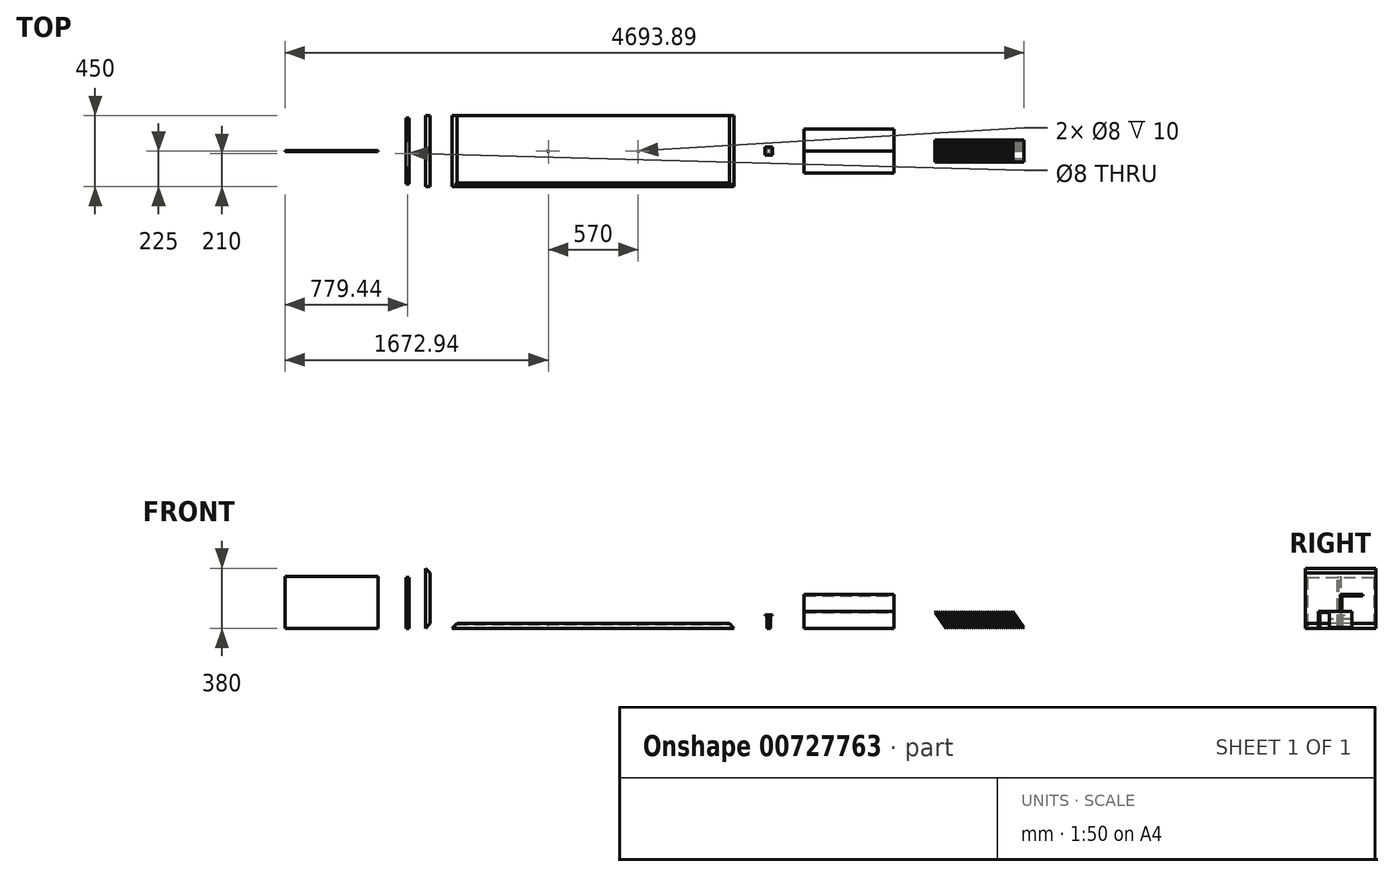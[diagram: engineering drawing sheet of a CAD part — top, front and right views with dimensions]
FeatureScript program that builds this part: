
annotation { "Feature Type Name" : "Feature", "Feature Type Description" : "" }
export const myFeature = defineFeature(function(context is Context, id is Id, definition is map)
    precondition{}
    {
        {
            var Q0;
            Q0=qCreatedBy(makeId("Top.planeOp"),FACE);
            var sketch = newSketch(context, id + "F0", { "sketchPlane" : qUnion([Q0])});
            skLineSegment(sketch, "E0.bottom", {"start": v(-895, -225) * mm, "end": v(895, -225) * mm});
            skLineSegment(sketch, "E0.top", {"start": v(-895, 225) * mm, "end": v(895, 225) * mm});
            skLineSegment(sketch, "E0.left", {"start": v(-895, -225) * mm, "end": v(-895, 225) * mm});
            skLineSegment(sketch, "E0.right", {"start": v(895, -225) * mm, "end": v(895, 225) * mm});
            skPoint(sketch, "E0.middle", {"position": v(0, 0) * mm});
            skSolve(sketch);
        }
        {
            var Q0;
            Q0 = qSketchRegion(id + "F0", true);
            extrude(context, id + "F1", {"entities" : qUnion([Q0]), "depth" : 29 * mm, "offsetDistance" : 25 * mm});
        }
        {
            var Q0;
            Q0=makeQuery(id+"F1.opExtrude","SWEPT_FACE",FACE,{"disambiguationData":[OSD([sQuery(id+"F0.wireOp",EDGE,"E0.bottom")])]});
            var sketch = newSketch(context, id + "F2", { "sketchPlane" : qUnion([Q0])});
            skLineSegment(sketch, "E1", {"start": v(-895, 0) * mm, "end": v(-895, 29) * mm});
            skLineSegment(sketch, "E2", {"start": v(-895, 29) * mm, "end": v(-866, 29) * mm});
            skLineSegment(sketch, "E3", {"start": v(-866, 29) * mm, "end": v(-895, 0) * mm});
            skLineSegment(sketch, "E4", {"start": v(895, 0) * mm, "end": v(895, 29) * mm});
            skLineSegment(sketch, "E5", {"start": v(895, 29) * mm, "end": v(866, 29) * mm});
            skLineSegment(sketch, "E6", {"start": v(866, 29) * mm, "end": v(895, 0) * mm});
            skSolve(sketch);
        }
        {
            var Q0;
            Q0 = qSketchRegion(id + "F2", true);
            extrude(context, id + "F3", {"entities" : qUnion([Q0]), "operationType" : NewBodyOperationType.REMOVE, "oppositeDirection" : true, "depth" : 450 * mm, "offsetDistance" : 25 * mm});
        }
        {
            var Q0;
            Q0=qCreatedBy(makeId("Right.planeOp"),FACE);
            var sketch = newSketch(context, id + "F4", { "sketchPlane" : qUnion([Q0])});
            skLineSegment(sketch, "E7.bottom", {"start": v(-220, 29) * mm, "end": v(-202, 29) * mm});
            skLineSegment(sketch, "E7.top", {"start": v(-220, 24) * mm, "end": v(-202, 24) * mm});
            skLineSegment(sketch, "E7.left", {"start": v(-220, 29) * mm, "end": v(-220, 24) * mm});
            skLineSegment(sketch, "E7.right", {"start": v(-202, 29) * mm, "end": v(-202, 24) * mm});
            skSolve(sketch);
        }
        {
            var Q0;
            Q0 = qSketchRegion(id + "F4", true);
            extrude(context, id + "F5", {"entities" : qUnion([Q0]), "operationType" : NewBodyOperationType.REMOVE, "oppositeDirection" : true, "depth" : 1790 * mm, "offsetDistance" : 25 * mm, "symmetric" : true});
        }
        {
            var Q0;
            {var subQ0=sQuery(id+"F0.wireOp",EDGE,"E0.top");Q0=makeQuery(id+"F5.boolean.opBoolean","SPLIT",FACE,{"disambiguationData":[TD([makeQuery(id+"F1.opExtrude","SWEPT_FACE",FACE,{"disambiguationData":[OSD([subQ0])]})])],"derivedFrom":makeQuery(id+"F1.opExtrude","CAP_FACE",FACE,{"disambiguationData":[OSD([sQuery(id+"F0.wireOp",EDGE,"E0.bottom"),subQ0,sQuery(id+"F0.wireOp",EDGE,"E0.left"),sQuery(id+"F0.wireOp",EDGE,"E0.right")])],"isStart":false})});}
            var sketch = newSketch(context, id + "F6", { "sketchPlane" : qUnion([Q0])});
            skCircle(sketch, "E8", {"center": v(-285, 0) * mm, "radius": 4 * mm});
            skCircle(sketch, "E9", {"center": v(285, 0) * mm, "radius": 4 * mm});
            skSolve(sketch);
        }
        {
            var Q0;
            Q0 = qSketchRegion(id + "F6", true);
            extrude(context, id + "F7", {"entities" : qUnion([Q0]), "operationType" : NewBodyOperationType.REMOVE, "oppositeDirection" : true, "depth" : 10 * mm, "offsetDistance" : 25 * mm});
        }
        {
            var Q0;
            Q0=qCreatedBy(makeId("Top.planeOp"),FACE);
            var sketch = newSketch(context, id + "F8", { "sketchPlane" : qUnion([Q0])});
            skLineSegment(sketch, "E10.bottom", {"start": v(-1064.12, -225) * mm, "end": v(-1035.12, -225) * mm});
            skLineSegment(sketch, "E10.top", {"start": v(-1064.12, 225) * mm, "end": v(-1035.12, 225) * mm});
            skLineSegment(sketch, "E10.left", {"start": v(-1064.12, -225) * mm, "end": v(-1064.12, 225) * mm});
            skLineSegment(sketch, "E10.right", {"start": v(-1035.12, -225) * mm, "end": v(-1035.12, 225) * mm});
            skPoint(sketch, "E10.middle", {"position": v(-1049.62, 0) * mm});
            skSolve(sketch);
        }
        {
            var Q0;
            Q0 = qSketchRegion(id + "F8", true);
            extrude(context, id + "F9", {"entities" : qUnion([Q0]), "depth" : 380 * mm, "offsetDistance" : 25 * mm});
        }
        {
            var Q0;
            Q0=makeQuery(id+"F9.opExtrude","SWEPT_FACE",FACE,{"disambiguationData":[OSD([sQuery(id+"F8.wireOp",EDGE,"E10.bottom")])]});
            var sketch = newSketch(context, id + "F10", { "sketchPlane" : qUnion([Q0])});
            skLineSegment(sketch, "E11", {"start": v(-1035.12, 380) * mm, "end": v(-1064.12, 380) * mm});
            skLineSegment(sketch, "E12", {"start": v(-1035.12, 380) * mm, "end": v(-1035.12, 351) * mm});
            skLineSegment(sketch, "E13", {"start": v(-1035.12, 351) * mm, "end": v(-1064.12, 380) * mm});
            skLineSegment(sketch, "E14", {"start": v(-1064.12, 0) * mm, "end": v(-1035.12, 0) * mm});
            skLineSegment(sketch, "E15", {"start": v(-1035.12, 0) * mm, "end": v(-1035.12, 29) * mm});
            skLineSegment(sketch, "E16", {"start": v(-1035.12, 29) * mm, "end": v(-1064.12, 0) * mm});
            skSolve(sketch);
        }
        {
            var Q0;
            Q0 = qSketchRegion(id + "F10", true);
            extrude(context, id + "F11", {"entities" : qUnion([Q0]), "operationType" : NewBodyOperationType.REMOVE, "oppositeDirection" : true, "depth" : 450 * mm, "offsetDistance" : 25 * mm});
        }
        {
            var Q0;
            Q0=qCreatedBy(makeId("Top.planeOp"),FACE);
            var sketch = newSketch(context, id + "F12", { "sketchPlane" : qUnion([Q0])});
            skLineSegment(sketch, "E17.bottom", {"start": v(-1188.5, -210) * mm, "end": v(-1168.5, -210) * mm});
            skLineSegment(sketch, "E17.top", {"start": v(-1188.5, 210) * mm, "end": v(-1168.5, 210) * mm});
            skLineSegment(sketch, "E17.left", {"start": v(-1188.5, -210) * mm, "end": v(-1188.5, 210) * mm});
            skLineSegment(sketch, "E17.right", {"start": v(-1168.5, -210) * mm, "end": v(-1168.5, 210) * mm});
            skPoint(sketch, "E17.middle", {"position": v(-1178.5, 0) * mm});
            skSolve(sketch);
        }
        {
            var Q0;
            Q0 = qSketchRegion(id + "F12", true);
            extrude(context, id + "F13", {"entities" : qUnion([Q0]), "depth" : 322 * mm, "offsetDistance" : 25 * mm});
        }
        {
            var Q0;
            Q0=makeQuery(id+"F13.opExtrude","CAP_FACE",FACE,{"disambiguationData":[OSD([sQuery(id+"F12.wireOp",EDGE,"E17.bottom"),sQuery(id+"F12.wireOp",EDGE,"E17.top"),sQuery(id+"F12.wireOp",EDGE,"E17.left"),sQuery(id+"F12.wireOp",EDGE,"E17.right")])],"isStart":false});
            var sketch = newSketch(context, id + "F14", { "sketchPlane" : qUnion([Q0])});
            skCircle(sketch, "E18", {"center": v(-1178.5, -15) * mm, "radius": 4 * mm});
            skPoint(sketch, "E18.centerSnap0", {"position": v(-1178.5, 210) * mm});
            skSolve(sketch);
        }
        {
            var Q0;
            Q0 = qSketchRegion(id + "F14", true);
            extrude(context, id + "F15", {"entities" : qUnion([Q0]), "operationType" : NewBodyOperationType.REMOVE, "oppositeDirection" : true, "depth" : 322 * mm, "offsetDistance" : 25 * mm});
        }
        {
            var Q0;
            Q0=qCreatedBy(makeId("Top.planeOp"),FACE);
            var sketch = newSketch(context, id + "F16", { "sketchPlane" : qUnion([Q0])});
            skLineSegment(sketch, "E19.bottom", {"start": v(1339.88, -140) * mm, "end": v(1910.88, -140) * mm});
            skLineSegment(sketch, "E19.top", {"start": v(1339.88, 140) * mm, "end": v(1910.88, 140) * mm});
            skLineSegment(sketch, "E19.left", {"start": v(1339.88, -140) * mm, "end": v(1339.88, 140) * mm});
            skLineSegment(sketch, "E19.right", {"start": v(1910.88, -140) * mm, "end": v(1910.88, 140) * mm});
            skPoint(sketch, "E19.middle", {"position": v(1625.38, 0) * mm});
            skSolve(sketch);
        }
        {
            var Q0;
            Q0 = qSketchRegion(id + "F16", true);
            extrude(context, id + "F17", {"entities" : qUnion([Q0]), "depth" : 322 * mm, "offsetDistance" : 25 * mm});
        }
        {
            var Q0;
            Q0=makeQuery(id+"F17.opExtrude","SWEPT_FACE",FACE,{"disambiguationData":[OSD([sQuery(id+"F16.wireOp",EDGE,"E19.right")])]});
            var sketch = newSketch(context, id + "F18", { "sketchPlane" : qUnion([Q0])});
            skLineSegment(sketch, "E20", {"start": v(-140, 107) * mm, "end": v(0, 107) * mm});
            skLineSegment(sketch, "E21", {"start": v(0, 107) * mm, "end": v(0, 214) * mm});
            skLineSegment(sketch, "E22", {"start": v(0, 214) * mm, "end": v(140, 214) * mm});
            skLineSegment(sketch, "E23", {"start": v(140, 206) * mm, "end": v(8, 206) * mm});
            skLineSegment(sketch, "E24", {"start": v(8, 206) * mm, "end": v(8, 99) * mm});
            skLineSegment(sketch, "E25", {"start": v(8, 99) * mm, "end": v(-132, 99) * mm});
            skLineSegment(sketch, "E26", {"start": v(-132, 99) * mm, "end": v(-132, 0) * mm});
            skLineSegment(sketch, "E27", {"start": v(-132, 0) * mm, "end": v(140, 0) * mm});
            skLineSegment(sketch, "E28", {"start": v(140, 0) * mm, "end": v(140, 206) * mm});
            skLineSegment(sketch, "E29", {"start": v(140, 214) * mm, "end": v(140, 322) * mm});
            skLineSegment(sketch, "E30", {"start": v(140, 322) * mm, "end": v(-140, 322) * mm});
            skLineSegment(sketch, "E31", {"start": v(-140, 322) * mm, "end": v(-140, 107) * mm});
            skSolve(sketch);
        }
        {
            var Q0;
            Q0 = qSketchRegion(id + "F18", true);
            extrude(context, id + "F19", {"entities" : qUnion([Q0]), "operationType" : NewBodyOperationType.REMOVE, "oppositeDirection" : true, "depth" : 571 * mm, "offsetDistance" : 25 * mm});
        }
        {
            var Q0;
            Q0=qCreatedBy(makeId("Top.planeOp"),FACE);
            var sketch = newSketch(context, id + "F20", { "sketchPlane" : qUnion([Q0])});
            skLineSegment(sketch, "E32.bottom", {"start": v(2170.09, -70) * mm, "end": v(2741.09, -70) * mm});
            skLineSegment(sketch, "E32.top", {"start": v(2170.09, 70) * mm, "end": v(2741.09, 70) * mm});
            skLineSegment(sketch, "E32.left", {"start": v(2170.09, -70) * mm, "end": v(2170.09, 70) * mm});
            skLineSegment(sketch, "E32.right", {"start": v(2741.09, -70) * mm, "end": v(2741.09, 70) * mm});
            skPoint(sketch, "E32.middle", {"position": v(2455.59, 0) * mm});
            skSolve(sketch);
        }
        {
            var Q0;
            Q0 = qSketchRegion(id + "F20", true);
            extrude(context, id + "F21", {"entities" : qUnion([Q0]), "depth" : 107 * mm, "offsetDistance" : 25 * mm});
        }
        {
            var Q0;
            Q0=makeQuery(id+"F21.opExtrude","SWEPT_FACE",FACE,{"disambiguationData":[OSD([sQuery(id+"F20.wireOp",EDGE,"E32.bottom")])]});
            var sketch = newSketch(context, id + "F22", { "sketchPlane" : qUnion([Q0])});
            skLineSegment(sketch, "E33", {"start": v(2170.09, 101.15) * mm, "end": v(2241.81, 0) * mm});
            skLineSegment(sketch, "E34", {"start": v(2170.09, 101.15) * mm, "end": v(2178.25, 106.94) * mm});
            skLineSegment(sketch, "E35", {"start": v(2249.97, 5.78) * mm, "end": v(2241.81, 0) * mm});
            skLineSegment(sketch, "E36", {"start": v(2178.25, 106.94) * mm, "end": v(2213.53, 57.18) * mm});
            skLineSegment(sketch, "E37", {"start": v(2249.97, 5.78) * mm, "end": v(2214.69, 55.54) * mm});
            skLineSegment(sketch, "E38", {"start": v(2214.69, 55.54) * mm, "end": v(2215.5, 56.12) * mm});
            skLineSegment(sketch, "E39", {"start": v(2213.53, 57.18) * mm, "end": v(2214.35, 57.75) * mm});
            skLineSegment(sketch, "E40", {"start": v(2214.35, 57.75) * mm, "end": v(2183.57, 101.15) * mm});
            skLineSegment(sketch, "E41", {"start": v(2183.57, 101.15) * mm, "end": v(2191.73, 106.94) * mm});
            skLineSegment(sketch, "E42", {"start": v(2191.73, 106.94) * mm, "end": v(2227.01, 57.18) * mm});
            skLineSegment(sketch, "E43", {"start": v(2215.5, 56.12) * mm, "end": v(2255.3, 0) * mm});
            skLineSegment(sketch, "E44", {"start": v(2255.3, 0) * mm, "end": v(2263.45, 5.78) * mm});
            skLineSegment(sketch, "E45", {"start": v(2263.45, 5.78) * mm, "end": v(2228.17, 55.54) * mm});
            skLineSegment(sketch, "E46.1.0.0", {"start": v(2227.85, 57.75) * mm, "end": v(2197.07, 101.15) * mm});
            skLineSegment(sketch, "E46.1.0.1", {"start": v(2205.23, 106.94) * mm, "end": v(2240.51, 57.18) * mm});
            skLineSegment(sketch, "E46.1.0.2", {"start": v(2229, 56.12) * mm, "end": v(2268.8, 0) * mm});
            skLineSegment(sketch, "E46.1.0.3", {"start": v(2276.95, 5.78) * mm, "end": v(2241.67, 55.54) * mm});
            skLineSegment(sketch, "E46.1.0.4", {"start": v(2268.8, 0) * mm, "end": v(2276.95, 5.78) * mm});
            skLineSegment(sketch, "E46.1.0.5", {"start": v(2197.07, 101.15) * mm, "end": v(2205.23, 106.94) * mm});
            skLineSegment(sketch, "E46.2.0.0", {"start": v(2241.35, 57.75) * mm, "end": v(2210.57, 101.15) * mm});
            skLineSegment(sketch, "E46.2.0.1", {"start": v(2218.73, 106.94) * mm, "end": v(2254.01, 57.18) * mm});
            skLineSegment(sketch, "E46.2.0.2", {"start": v(2242.5, 56.12) * mm, "end": v(2282.3, 0) * mm});
            skLineSegment(sketch, "E46.2.0.3", {"start": v(2290.45, 5.78) * mm, "end": v(2255.17, 55.54) * mm});
            skLineSegment(sketch, "E46.2.0.4", {"start": v(2282.3, 0) * mm, "end": v(2290.45, 5.78) * mm});
            skLineSegment(sketch, "E46.2.0.5", {"start": v(2210.57, 101.15) * mm, "end": v(2218.73, 106.94) * mm});
            skLineSegment(sketch, "E46.3.0.0", {"start": v(2254.85, 57.75) * mm, "end": v(2224.07, 101.15) * mm});
            skLineSegment(sketch, "E46.3.0.1", {"start": v(2232.23, 106.94) * mm, "end": v(2267.51, 57.18) * mm});
            skLineSegment(sketch, "E46.3.0.2", {"start": v(2256, 56.12) * mm, "end": v(2295.8, 0) * mm});
            skLineSegment(sketch, "E46.3.0.3", {"start": v(2303.95, 5.78) * mm, "end": v(2268.67, 55.54) * mm});
            skLineSegment(sketch, "E46.3.0.4", {"start": v(2295.8, 0) * mm, "end": v(2303.95, 5.78) * mm});
            skLineSegment(sketch, "E46.3.0.5", {"start": v(2224.07, 101.15) * mm, "end": v(2232.23, 106.94) * mm});
            skLineSegment(sketch, "E46.4.0.0", {"start": v(2268.35, 57.75) * mm, "end": v(2237.57, 101.15) * mm});
            skLineSegment(sketch, "E46.4.0.1", {"start": v(2245.73, 106.94) * mm, "end": v(2281.01, 57.18) * mm});
            skLineSegment(sketch, "E46.4.0.2", {"start": v(2269.5, 56.12) * mm, "end": v(2309.3, 0) * mm});
            skLineSegment(sketch, "E46.4.0.3", {"start": v(2317.45, 5.78) * mm, "end": v(2282.17, 55.54) * mm});
            skLineSegment(sketch, "E46.4.0.4", {"start": v(2309.3, 0) * mm, "end": v(2317.45, 5.78) * mm});
            skLineSegment(sketch, "E46.4.0.5", {"start": v(2237.57, 101.15) * mm, "end": v(2245.73, 106.94) * mm});
            skLineSegment(sketch, "E46.5.0.0", {"start": v(2281.85, 57.75) * mm, "end": v(2251.07, 101.15) * mm});
            skLineSegment(sketch, "E46.5.0.1", {"start": v(2259.23, 106.94) * mm, "end": v(2294.51, 57.18) * mm});
            skLineSegment(sketch, "E46.5.0.2", {"start": v(2283, 56.12) * mm, "end": v(2322.8, 0) * mm});
            skLineSegment(sketch, "E46.5.0.3", {"start": v(2330.95, 5.78) * mm, "end": v(2295.67, 55.54) * mm});
            skLineSegment(sketch, "E46.5.0.4", {"start": v(2322.8, 0) * mm, "end": v(2330.95, 5.78) * mm});
            skLineSegment(sketch, "E46.5.0.5", {"start": v(2251.07, 101.15) * mm, "end": v(2259.23, 106.94) * mm});
            skLineSegment(sketch, "E46.6.0.0", {"start": v(2295.35, 57.75) * mm, "end": v(2264.57, 101.15) * mm});
            skLineSegment(sketch, "E46.6.0.1", {"start": v(2272.73, 106.94) * mm, "end": v(2308.01, 57.18) * mm});
            skLineSegment(sketch, "E46.6.0.2", {"start": v(2296.5, 56.12) * mm, "end": v(2336.3, 0) * mm});
            skLineSegment(sketch, "E46.6.0.3", {"start": v(2344.45, 5.78) * mm, "end": v(2309.17, 55.54) * mm});
            skLineSegment(sketch, "E46.6.0.4", {"start": v(2336.3, 0) * mm, "end": v(2344.45, 5.78) * mm});
            skLineSegment(sketch, "E46.6.0.5", {"start": v(2264.57, 101.15) * mm, "end": v(2272.73, 106.94) * mm});
            skLineSegment(sketch, "E46.7.0.0", {"start": v(2308.85, 57.75) * mm, "end": v(2278.07, 101.15) * mm});
            skLineSegment(sketch, "E46.7.0.1", {"start": v(2286.23, 106.94) * mm, "end": v(2321.51, 57.18) * mm});
            skLineSegment(sketch, "E46.7.0.2", {"start": v(2310, 56.12) * mm, "end": v(2349.8, 0) * mm});
            skLineSegment(sketch, "E46.7.0.3", {"start": v(2357.95, 5.78) * mm, "end": v(2322.67, 55.54) * mm});
            skLineSegment(sketch, "E46.7.0.4", {"start": v(2349.8, 0) * mm, "end": v(2357.95, 5.78) * mm});
            skLineSegment(sketch, "E46.7.0.5", {"start": v(2278.07, 101.15) * mm, "end": v(2286.23, 106.94) * mm});
            skLineSegment(sketch, "E46.8.0.0", {"start": v(2322.35, 57.75) * mm, "end": v(2291.57, 101.15) * mm});
            skLineSegment(sketch, "E46.8.0.1", {"start": v(2299.73, 106.94) * mm, "end": v(2335.01, 57.18) * mm});
            skLineSegment(sketch, "E46.8.0.2", {"start": v(2323.5, 56.12) * mm, "end": v(2363.3, 0) * mm});
            skLineSegment(sketch, "E46.8.0.3", {"start": v(2371.45, 5.78) * mm, "end": v(2336.17, 55.54) * mm});
            skLineSegment(sketch, "E46.8.0.4", {"start": v(2363.3, 0) * mm, "end": v(2371.45, 5.78) * mm});
            skLineSegment(sketch, "E46.8.0.5", {"start": v(2291.57, 101.15) * mm, "end": v(2299.73, 106.94) * mm});
            skLineSegment(sketch, "E46.9.0.0", {"start": v(2335.85, 57.75) * mm, "end": v(2305.07, 101.15) * mm});
            skLineSegment(sketch, "E46.9.0.1", {"start": v(2313.23, 106.94) * mm, "end": v(2348.51, 57.18) * mm});
            skLineSegment(sketch, "E46.9.0.2", {"start": v(2337, 56.12) * mm, "end": v(2376.8, 0) * mm});
            skLineSegment(sketch, "E46.9.0.3", {"start": v(2384.95, 5.78) * mm, "end": v(2349.67, 55.54) * mm});
            skLineSegment(sketch, "E46.9.0.4", {"start": v(2376.8, 0) * mm, "end": v(2384.95, 5.78) * mm});
            skLineSegment(sketch, "E46.9.0.5", {"start": v(2305.07, 101.15) * mm, "end": v(2313.23, 106.94) * mm});
            skLineSegment(sketch, "E46.10.0.0", {"start": v(2349.35, 57.75) * mm, "end": v(2318.57, 101.15) * mm});
            skLineSegment(sketch, "E46.10.0.1", {"start": v(2326.73, 106.94) * mm, "end": v(2362.01, 57.18) * mm});
            skLineSegment(sketch, "E46.10.0.2", {"start": v(2350.5, 56.12) * mm, "end": v(2390.3, 0) * mm});
            skLineSegment(sketch, "E46.10.0.3", {"start": v(2398.45, 5.78) * mm, "end": v(2363.17, 55.54) * mm});
            skLineSegment(sketch, "E46.10.0.4", {"start": v(2390.3, 0) * mm, "end": v(2398.45, 5.78) * mm});
            skLineSegment(sketch, "E46.10.0.5", {"start": v(2318.57, 101.15) * mm, "end": v(2326.73, 106.94) * mm});
            skLineSegment(sketch, "E46.11.0.0", {"start": v(2362.85, 57.75) * mm, "end": v(2332.07, 101.15) * mm});
            skLineSegment(sketch, "E46.11.0.1", {"start": v(2340.23, 106.94) * mm, "end": v(2375.51, 57.18) * mm});
            skLineSegment(sketch, "E46.11.0.2", {"start": v(2364, 56.12) * mm, "end": v(2403.8, 0) * mm});
            skLineSegment(sketch, "E46.11.0.3", {"start": v(2411.95, 5.78) * mm, "end": v(2376.67, 55.54) * mm});
            skLineSegment(sketch, "E46.11.0.4", {"start": v(2403.8, 0) * mm, "end": v(2411.95, 5.78) * mm});
            skLineSegment(sketch, "E46.11.0.5", {"start": v(2332.07, 101.15) * mm, "end": v(2340.23, 106.94) * mm});
            skLineSegment(sketch, "E46.12.0.0", {"start": v(2376.35, 57.75) * mm, "end": v(2345.57, 101.15) * mm});
            skLineSegment(sketch, "E46.12.0.1", {"start": v(2353.73, 106.94) * mm, "end": v(2389.01, 57.18) * mm});
            skLineSegment(sketch, "E46.12.0.2", {"start": v(2377.5, 56.12) * mm, "end": v(2417.3, 0) * mm});
            skLineSegment(sketch, "E46.12.0.3", {"start": v(2425.45, 5.78) * mm, "end": v(2390.17, 55.54) * mm});
            skLineSegment(sketch, "E46.12.0.4", {"start": v(2417.3, 0) * mm, "end": v(2425.45, 5.78) * mm});
            skLineSegment(sketch, "E46.12.0.5", {"start": v(2345.57, 101.15) * mm, "end": v(2353.73, 106.94) * mm});
            skLineSegment(sketch, "E46.13.0.0", {"start": v(2389.85, 57.75) * mm, "end": v(2359.07, 101.15) * mm});
            skLineSegment(sketch, "E46.13.0.1", {"start": v(2367.23, 106.94) * mm, "end": v(2402.51, 57.18) * mm});
            skLineSegment(sketch, "E46.13.0.2", {"start": v(2391, 56.12) * mm, "end": v(2430.8, 0) * mm});
            skLineSegment(sketch, "E46.13.0.3", {"start": v(2438.95, 5.78) * mm, "end": v(2403.67, 55.54) * mm});
            skLineSegment(sketch, "E46.13.0.4", {"start": v(2430.8, 0) * mm, "end": v(2438.95, 5.78) * mm});
            skLineSegment(sketch, "E46.13.0.5", {"start": v(2359.07, 101.15) * mm, "end": v(2367.23, 106.94) * mm});
            skLineSegment(sketch, "E46.14.0.0", {"start": v(2403.35, 57.75) * mm, "end": v(2372.57, 101.15) * mm});
            skLineSegment(sketch, "E46.14.0.1", {"start": v(2380.73, 106.94) * mm, "end": v(2416.01, 57.18) * mm});
            skLineSegment(sketch, "E46.14.0.2", {"start": v(2404.5, 56.12) * mm, "end": v(2444.3, 0) * mm});
            skLineSegment(sketch, "E46.14.0.3", {"start": v(2452.45, 5.78) * mm, "end": v(2417.17, 55.54) * mm});
            skLineSegment(sketch, "E46.14.0.4", {"start": v(2444.3, 0) * mm, "end": v(2452.45, 5.78) * mm});
            skLineSegment(sketch, "E46.14.0.5", {"start": v(2372.57, 101.15) * mm, "end": v(2380.73, 106.94) * mm});
            skLineSegment(sketch, "E46.15.0.0", {"start": v(2416.85, 57.75) * mm, "end": v(2386.07, 101.15) * mm});
            skLineSegment(sketch, "E46.15.0.1", {"start": v(2394.23, 106.94) * mm, "end": v(2429.51, 57.18) * mm});
            skLineSegment(sketch, "E46.15.0.2", {"start": v(2418, 56.12) * mm, "end": v(2457.8, 0) * mm});
            skLineSegment(sketch, "E46.15.0.3", {"start": v(2465.95, 5.78) * mm, "end": v(2430.67, 55.54) * mm});
            skLineSegment(sketch, "E46.15.0.4", {"start": v(2457.8, 0) * mm, "end": v(2465.95, 5.78) * mm});
            skLineSegment(sketch, "E46.15.0.5", {"start": v(2386.07, 101.15) * mm, "end": v(2394.23, 106.94) * mm});
            skLineSegment(sketch, "E46.16.0.0", {"start": v(2430.35, 57.75) * mm, "end": v(2399.57, 101.15) * mm});
            skLineSegment(sketch, "E46.16.0.1", {"start": v(2407.73, 106.94) * mm, "end": v(2443.01, 57.18) * mm});
            skLineSegment(sketch, "E46.16.0.2", {"start": v(2431.5, 56.12) * mm, "end": v(2471.3, 0) * mm});
            skLineSegment(sketch, "E46.16.0.3", {"start": v(2479.45, 5.78) * mm, "end": v(2444.17, 55.54) * mm});
            skLineSegment(sketch, "E46.16.0.4", {"start": v(2471.3, 0) * mm, "end": v(2479.45, 5.78) * mm});
            skLineSegment(sketch, "E46.16.0.5", {"start": v(2399.57, 101.15) * mm, "end": v(2407.73, 106.94) * mm});
            skLineSegment(sketch, "E46.17.0.0", {"start": v(2443.85, 57.75) * mm, "end": v(2413.07, 101.15) * mm});
            skLineSegment(sketch, "E46.17.0.1", {"start": v(2421.23, 106.94) * mm, "end": v(2456.51, 57.18) * mm});
            skLineSegment(sketch, "E46.17.0.2", {"start": v(2445, 56.12) * mm, "end": v(2484.8, 0) * mm});
            skLineSegment(sketch, "E46.17.0.3", {"start": v(2492.95, 5.78) * mm, "end": v(2457.67, 55.54) * mm});
            skLineSegment(sketch, "E46.17.0.4", {"start": v(2484.8, 0) * mm, "end": v(2492.95, 5.78) * mm});
            skLineSegment(sketch, "E46.17.0.5", {"start": v(2413.07, 101.15) * mm, "end": v(2421.23, 106.94) * mm});
            skLineSegment(sketch, "E46.18.0.0", {"start": v(2457.35, 57.75) * mm, "end": v(2426.57, 101.15) * mm});
            skLineSegment(sketch, "E46.18.0.1", {"start": v(2434.73, 106.94) * mm, "end": v(2470.01, 57.18) * mm});
            skLineSegment(sketch, "E46.18.0.2", {"start": v(2458.5, 56.12) * mm, "end": v(2498.3, 0) * mm});
            skLineSegment(sketch, "E46.18.0.3", {"start": v(2506.45, 5.78) * mm, "end": v(2471.17, 55.54) * mm});
            skLineSegment(sketch, "E46.18.0.4", {"start": v(2498.3, 0) * mm, "end": v(2506.45, 5.78) * mm});
            skLineSegment(sketch, "E46.18.0.5", {"start": v(2426.57, 101.15) * mm, "end": v(2434.73, 106.94) * mm});
            skLineSegment(sketch, "E46.19.0.0", {"start": v(2470.85, 57.75) * mm, "end": v(2440.07, 101.15) * mm});
            skLineSegment(sketch, "E46.19.0.1", {"start": v(2448.23, 106.94) * mm, "end": v(2483.51, 57.18) * mm});
            skLineSegment(sketch, "E46.19.0.2", {"start": v(2472, 56.12) * mm, "end": v(2511.8, 0) * mm});
            skLineSegment(sketch, "E46.19.0.3", {"start": v(2519.95, 5.78) * mm, "end": v(2484.67, 55.54) * mm});
            skLineSegment(sketch, "E46.19.0.4", {"start": v(2511.8, 0) * mm, "end": v(2519.95, 5.78) * mm});
            skLineSegment(sketch, "E46.19.0.5", {"start": v(2440.07, 101.15) * mm, "end": v(2448.23, 106.94) * mm});
            skLineSegment(sketch, "E46.20.0.0", {"start": v(2484.35, 57.75) * mm, "end": v(2453.57, 101.15) * mm});
            skLineSegment(sketch, "E46.20.0.1", {"start": v(2461.73, 106.94) * mm, "end": v(2497.01, 57.18) * mm});
            skLineSegment(sketch, "E46.20.0.2", {"start": v(2485.5, 56.12) * mm, "end": v(2525.3, 0) * mm});
            skLineSegment(sketch, "E46.20.0.3", {"start": v(2533.45, 5.78) * mm, "end": v(2498.17, 55.54) * mm});
            skLineSegment(sketch, "E46.20.0.4", {"start": v(2525.3, 0) * mm, "end": v(2533.45, 5.78) * mm});
            skLineSegment(sketch, "E46.20.0.5", {"start": v(2453.57, 101.15) * mm, "end": v(2461.73, 106.94) * mm});
            skLineSegment(sketch, "E46.21.0.0", {"start": v(2497.85, 57.75) * mm, "end": v(2467.07, 101.15) * mm});
            skLineSegment(sketch, "E46.21.0.1", {"start": v(2475.23, 106.94) * mm, "end": v(2510.51, 57.18) * mm});
            skLineSegment(sketch, "E46.21.0.2", {"start": v(2499, 56.12) * mm, "end": v(2538.8, 0) * mm});
            skLineSegment(sketch, "E46.21.0.3", {"start": v(2546.95, 5.78) * mm, "end": v(2511.67, 55.54) * mm});
            skLineSegment(sketch, "E46.21.0.4", {"start": v(2538.8, 0) * mm, "end": v(2546.95, 5.78) * mm});
            skLineSegment(sketch, "E46.21.0.5", {"start": v(2467.07, 101.15) * mm, "end": v(2475.23, 106.94) * mm});
            skLineSegment(sketch, "E46.22.0.0", {"start": v(2511.35, 57.75) * mm, "end": v(2480.57, 101.15) * mm});
            skLineSegment(sketch, "E46.22.0.1", {"start": v(2488.73, 106.94) * mm, "end": v(2524.01, 57.18) * mm});
            skLineSegment(sketch, "E46.22.0.2", {"start": v(2512.5, 56.12) * mm, "end": v(2552.3, 0) * mm});
            skLineSegment(sketch, "E46.22.0.3", {"start": v(2560.45, 5.78) * mm, "end": v(2525.17, 55.54) * mm});
            skLineSegment(sketch, "E46.22.0.4", {"start": v(2552.3, 0) * mm, "end": v(2560.45, 5.78) * mm});
            skLineSegment(sketch, "E46.22.0.5", {"start": v(2480.57, 101.15) * mm, "end": v(2488.73, 106.94) * mm});
            skLineSegment(sketch, "E46.23.0.0", {"start": v(2524.85, 57.75) * mm, "end": v(2494.07, 101.15) * mm});
            skLineSegment(sketch, "E46.23.0.1", {"start": v(2502.23, 106.94) * mm, "end": v(2537.51, 57.18) * mm});
            skLineSegment(sketch, "E46.23.0.2", {"start": v(2526, 56.12) * mm, "end": v(2565.8, 0) * mm});
            skLineSegment(sketch, "E46.23.0.3", {"start": v(2573.95, 5.78) * mm, "end": v(2538.67, 55.54) * mm});
            skLineSegment(sketch, "E46.23.0.4", {"start": v(2565.8, 0) * mm, "end": v(2573.95, 5.78) * mm});
            skLineSegment(sketch, "E46.23.0.5", {"start": v(2494.07, 101.15) * mm, "end": v(2502.23, 106.94) * mm});
            skLineSegment(sketch, "E46.24.0.0", {"start": v(2538.35, 57.75) * mm, "end": v(2507.57, 101.15) * mm});
            skLineSegment(sketch, "E46.24.0.1", {"start": v(2515.73, 106.94) * mm, "end": v(2551.01, 57.18) * mm});
            skLineSegment(sketch, "E46.24.0.2", {"start": v(2539.5, 56.12) * mm, "end": v(2579.3, 0) * mm});
            skLineSegment(sketch, "E46.24.0.3", {"start": v(2587.45, 5.78) * mm, "end": v(2552.17, 55.54) * mm});
            skLineSegment(sketch, "E46.24.0.4", {"start": v(2579.3, 0) * mm, "end": v(2587.45, 5.78) * mm});
            skLineSegment(sketch, "E46.24.0.5", {"start": v(2507.57, 101.15) * mm, "end": v(2515.73, 106.94) * mm});
            skLineSegment(sketch, "E46.25.0.0", {"start": v(2551.85, 57.75) * mm, "end": v(2521.07, 101.15) * mm});
            skLineSegment(sketch, "E46.25.0.1", {"start": v(2529.23, 106.94) * mm, "end": v(2564.51, 57.18) * mm});
            skLineSegment(sketch, "E46.25.0.2", {"start": v(2553, 56.12) * mm, "end": v(2592.8, 0) * mm});
            skLineSegment(sketch, "E46.25.0.3", {"start": v(2600.95, 5.78) * mm, "end": v(2565.67, 55.54) * mm});
            skLineSegment(sketch, "E46.25.0.4", {"start": v(2592.8, 0) * mm, "end": v(2600.95, 5.78) * mm});
            skLineSegment(sketch, "E46.25.0.5", {"start": v(2521.07, 101.15) * mm, "end": v(2529.23, 106.94) * mm});
            skLineSegment(sketch, "E46.26.0.0", {"start": v(2565.35, 57.75) * mm, "end": v(2534.57, 101.15) * mm});
            skLineSegment(sketch, "E46.26.0.1", {"start": v(2542.73, 106.94) * mm, "end": v(2578.01, 57.18) * mm});
            skLineSegment(sketch, "E46.26.0.2", {"start": v(2566.5, 56.12) * mm, "end": v(2606.3, 0) * mm});
            skLineSegment(sketch, "E46.26.0.3", {"start": v(2614.45, 5.78) * mm, "end": v(2579.17, 55.54) * mm});
            skLineSegment(sketch, "E46.26.0.4", {"start": v(2606.3, 0) * mm, "end": v(2614.45, 5.78) * mm});
            skLineSegment(sketch, "E46.26.0.5", {"start": v(2534.57, 101.15) * mm, "end": v(2542.73, 106.94) * mm});
            skLineSegment(sketch, "E46.27.0.0", {"start": v(2578.85, 57.75) * mm, "end": v(2548.07, 101.15) * mm});
            skLineSegment(sketch, "E46.27.0.1", {"start": v(2556.23, 106.94) * mm, "end": v(2591.51, 57.18) * mm});
            skLineSegment(sketch, "E46.27.0.2", {"start": v(2580, 56.12) * mm, "end": v(2619.8, 0) * mm});
            skLineSegment(sketch, "E46.27.0.3", {"start": v(2627.95, 5.78) * mm, "end": v(2592.67, 55.54) * mm});
            skLineSegment(sketch, "E46.27.0.4", {"start": v(2619.8, 0) * mm, "end": v(2627.95, 5.78) * mm});
            skLineSegment(sketch, "E46.27.0.5", {"start": v(2548.07, 101.15) * mm, "end": v(2556.23, 106.94) * mm});
            skLineSegment(sketch, "E46.28.0.0", {"start": v(2592.35, 57.75) * mm, "end": v(2561.57, 101.15) * mm});
            skLineSegment(sketch, "E46.28.0.1", {"start": v(2569.73, 106.94) * mm, "end": v(2605.01, 57.18) * mm});
            skLineSegment(sketch, "E46.28.0.2", {"start": v(2593.5, 56.12) * mm, "end": v(2633.3, 0) * mm});
            skLineSegment(sketch, "E46.28.0.3", {"start": v(2641.45, 5.78) * mm, "end": v(2606.17, 55.54) * mm});
            skLineSegment(sketch, "E46.28.0.4", {"start": v(2633.3, 0) * mm, "end": v(2641.45, 5.78) * mm});
            skLineSegment(sketch, "E46.28.0.5", {"start": v(2561.57, 101.15) * mm, "end": v(2569.73, 106.94) * mm});
            skLineSegment(sketch, "E46.29.0.0", {"start": v(2605.85, 57.75) * mm, "end": v(2575.07, 101.15) * mm});
            skLineSegment(sketch, "E46.29.0.1", {"start": v(2583.23, 106.94) * mm, "end": v(2618.51, 57.18) * mm});
            skLineSegment(sketch, "E46.29.0.2", {"start": v(2607, 56.12) * mm, "end": v(2646.8, 0) * mm});
            skLineSegment(sketch, "E46.29.0.3", {"start": v(2654.95, 5.78) * mm, "end": v(2619.67, 55.54) * mm});
            skLineSegment(sketch, "E46.29.0.4", {"start": v(2646.8, 0) * mm, "end": v(2654.95, 5.78) * mm});
            skLineSegment(sketch, "E46.29.0.5", {"start": v(2575.07, 101.15) * mm, "end": v(2583.23, 106.94) * mm});
            skLineSegment(sketch, "E46.30.0.0", {"start": v(2619.35, 57.75) * mm, "end": v(2588.57, 101.15) * mm});
            skLineSegment(sketch, "E46.30.0.1", {"start": v(2596.73, 106.94) * mm, "end": v(2632.01, 57.18) * mm});
            skLineSegment(sketch, "E46.30.0.2", {"start": v(2620.5, 56.12) * mm, "end": v(2660.3, 0) * mm});
            skLineSegment(sketch, "E46.30.0.3", {"start": v(2668.45, 5.78) * mm, "end": v(2633.17, 55.54) * mm});
            skLineSegment(sketch, "E46.30.0.4", {"start": v(2660.3, 0) * mm, "end": v(2668.45, 5.78) * mm});
            skLineSegment(sketch, "E46.30.0.5", {"start": v(2588.57, 101.15) * mm, "end": v(2596.73, 106.94) * mm});
            skLineSegment(sketch, "E46.31.0.0", {"start": v(2632.85, 57.75) * mm, "end": v(2602.07, 101.15) * mm});
            skLineSegment(sketch, "E46.31.0.1", {"start": v(2610.23, 106.94) * mm, "end": v(2645.51, 57.18) * mm});
            skLineSegment(sketch, "E46.31.0.2", {"start": v(2634, 56.12) * mm, "end": v(2673.8, 0) * mm});
            skLineSegment(sketch, "E46.31.0.3", {"start": v(2681.95, 5.78) * mm, "end": v(2646.67, 55.54) * mm});
            skLineSegment(sketch, "E46.31.0.4", {"start": v(2673.8, 0) * mm, "end": v(2681.95, 5.78) * mm});
            skLineSegment(sketch, "E46.31.0.5", {"start": v(2602.07, 101.15) * mm, "end": v(2610.23, 106.94) * mm});
            skLineSegment(sketch, "E46.32.0.0", {"start": v(2646.35, 57.75) * mm, "end": v(2615.57, 101.15) * mm});
            skLineSegment(sketch, "E46.32.0.1", {"start": v(2623.73, 106.94) * mm, "end": v(2659.01, 57.18) * mm});
            skLineSegment(sketch, "E46.32.0.2", {"start": v(2647.5, 56.12) * mm, "end": v(2687.3, 0) * mm});
            skLineSegment(sketch, "E46.32.0.3", {"start": v(2695.45, 5.78) * mm, "end": v(2660.17, 55.54) * mm});
            skLineSegment(sketch, "E46.32.0.4", {"start": v(2687.3, 0) * mm, "end": v(2695.45, 5.78) * mm});
            skLineSegment(sketch, "E46.32.0.5", {"start": v(2615.57, 101.15) * mm, "end": v(2623.73, 106.94) * mm});
            skLineSegment(sketch, "E46.33.0.0", {"start": v(2659.85, 57.75) * mm, "end": v(2629.07, 101.15) * mm});
            skLineSegment(sketch, "E46.33.0.1", {"start": v(2637.23, 106.94) * mm, "end": v(2672.51, 57.18) * mm});
            skLineSegment(sketch, "E46.33.0.2", {"start": v(2661, 56.12) * mm, "end": v(2700.8, 0) * mm});
            skLineSegment(sketch, "E46.33.0.3", {"start": v(2708.95, 5.78) * mm, "end": v(2673.67, 55.54) * mm});
            skLineSegment(sketch, "E46.33.0.4", {"start": v(2700.8, 0) * mm, "end": v(2708.95, 5.78) * mm});
            skLineSegment(sketch, "E46.33.0.5", {"start": v(2629.07, 101.15) * mm, "end": v(2637.23, 106.94) * mm});
            skLineSegment(sketch, "E46.34.0.0", {"start": v(2673.35, 57.75) * mm, "end": v(2642.57, 101.15) * mm});
            skLineSegment(sketch, "E46.34.0.1", {"start": v(2650.73, 106.94) * mm, "end": v(2686.01, 57.18) * mm});
            skLineSegment(sketch, "E46.34.0.2", {"start": v(2674.5, 56.12) * mm, "end": v(2714.3, 0) * mm});
            skLineSegment(sketch, "E46.34.0.3", {"start": v(2722.45, 5.78) * mm, "end": v(2687.17, 55.54) * mm});
            skLineSegment(sketch, "E46.34.0.4", {"start": v(2714.3, 0) * mm, "end": v(2722.45, 5.78) * mm});
            skLineSegment(sketch, "E46.34.0.5", {"start": v(2642.57, 101.15) * mm, "end": v(2650.73, 106.94) * mm});
            skLineSegment(sketch, "E46.35.0.0", {"start": v(2686.85, 57.75) * mm, "end": v(2656.07, 101.15) * mm});
            skLineSegment(sketch, "E46.35.0.1", {"start": v(2664.23, 106.94) * mm, "end": v(2699.51, 57.18) * mm});
            skLineSegment(sketch, "E46.35.0.2", {"start": v(2688, 56.12) * mm, "end": v(2727.8, 0) * mm});
            skLineSegment(sketch, "E46.35.0.3", {"start": v(2735.95, 5.78) * mm, "end": v(2700.67, 55.54) * mm});
            skLineSegment(sketch, "E46.35.0.4", {"start": v(2727.8, 0) * mm, "end": v(2735.95, 5.78) * mm});
            skLineSegment(sketch, "E46.35.0.5", {"start": v(2656.07, 101.15) * mm, "end": v(2664.23, 106.94) * mm});
            skLineSegment(sketch, "E46.direction1", {"start": v(2214.35, 57.75) * mm, "end": v(2227.85, 57.75) * mm, "construction": true});
            skLineSegment(sketch, "E47", {"start": v(2227.01, 57.18) * mm, "end": v(2227.85, 57.75) * mm});
            skLineSegment(sketch, "E48", {"start": v(2228.17, 55.54) * mm, "end": v(2229, 56.12) * mm});
            skLineSegment(sketch, "E49", {"start": v(2240.51, 57.18) * mm, "end": v(2241.35, 57.75) * mm});
            skLineSegment(sketch, "E50", {"start": v(2241.67, 55.54) * mm, "end": v(2242.5, 56.12) * mm});
            skLineSegment(sketch, "E51.1.0.0", {"start": v(2254.01, 57.18) * mm, "end": v(2254.85, 57.75) * mm});
            skLineSegment(sketch, "E51.1.0.1", {"start": v(2255.17, 55.54) * mm, "end": v(2256, 56.12) * mm});
            skLineSegment(sketch, "E51.2.0.0", {"start": v(2267.51, 57.18) * mm, "end": v(2268.35, 57.75) * mm});
            skLineSegment(sketch, "E51.2.0.1", {"start": v(2268.67, 55.54) * mm, "end": v(2269.5, 56.12) * mm});
            skLineSegment(sketch, "E51.3.0.0", {"start": v(2281.01, 57.18) * mm, "end": v(2281.85, 57.75) * mm});
            skLineSegment(sketch, "E51.3.0.1", {"start": v(2282.17, 55.54) * mm, "end": v(2283, 56.12) * mm});
            skLineSegment(sketch, "E51.4.0.0", {"start": v(2294.51, 57.18) * mm, "end": v(2295.35, 57.75) * mm});
            skLineSegment(sketch, "E51.4.0.1", {"start": v(2295.67, 55.54) * mm, "end": v(2296.5, 56.12) * mm});
            skLineSegment(sketch, "E51.5.0.0", {"start": v(2308.01, 57.18) * mm, "end": v(2308.85, 57.75) * mm});
            skLineSegment(sketch, "E51.5.0.1", {"start": v(2309.17, 55.54) * mm, "end": v(2310, 56.12) * mm});
            skLineSegment(sketch, "E51.6.0.0", {"start": v(2321.51, 57.18) * mm, "end": v(2322.35, 57.75) * mm});
            skLineSegment(sketch, "E51.6.0.1", {"start": v(2322.67, 55.54) * mm, "end": v(2323.5, 56.12) * mm});
            skLineSegment(sketch, "E51.7.0.0", {"start": v(2335.01, 57.18) * mm, "end": v(2335.85, 57.75) * mm});
            skLineSegment(sketch, "E51.7.0.1", {"start": v(2336.17, 55.54) * mm, "end": v(2337, 56.12) * mm});
            skLineSegment(sketch, "E51.8.0.0", {"start": v(2348.51, 57.18) * mm, "end": v(2349.35, 57.75) * mm});
            skLineSegment(sketch, "E51.8.0.1", {"start": v(2349.67, 55.54) * mm, "end": v(2350.5, 56.12) * mm});
            skLineSegment(sketch, "E51.9.0.0", {"start": v(2362.01, 57.18) * mm, "end": v(2362.85, 57.75) * mm});
            skLineSegment(sketch, "E51.9.0.1", {"start": v(2363.17, 55.54) * mm, "end": v(2364, 56.12) * mm});
            skLineSegment(sketch, "E51.10.0.0", {"start": v(2375.51, 57.18) * mm, "end": v(2376.35, 57.75) * mm});
            skLineSegment(sketch, "E51.10.0.1", {"start": v(2376.67, 55.54) * mm, "end": v(2377.5, 56.12) * mm});
            skLineSegment(sketch, "E51.11.0.0", {"start": v(2389.01, 57.18) * mm, "end": v(2389.85, 57.75) * mm});
            skLineSegment(sketch, "E51.11.0.1", {"start": v(2390.17, 55.54) * mm, "end": v(2391, 56.12) * mm});
            skLineSegment(sketch, "E51.12.0.0", {"start": v(2402.51, 57.18) * mm, "end": v(2403.35, 57.75) * mm});
            skLineSegment(sketch, "E51.12.0.1", {"start": v(2403.67, 55.54) * mm, "end": v(2404.5, 56.12) * mm});
            skLineSegment(sketch, "E51.13.0.0", {"start": v(2416.01, 57.18) * mm, "end": v(2416.85, 57.75) * mm});
            skLineSegment(sketch, "E51.13.0.1", {"start": v(2417.17, 55.54) * mm, "end": v(2418, 56.12) * mm});
            skLineSegment(sketch, "E51.14.0.0", {"start": v(2429.51, 57.18) * mm, "end": v(2430.35, 57.75) * mm});
            skLineSegment(sketch, "E51.14.0.1", {"start": v(2430.67, 55.54) * mm, "end": v(2431.5, 56.12) * mm});
            skLineSegment(sketch, "E51.15.0.0", {"start": v(2443.01, 57.18) * mm, "end": v(2443.85, 57.75) * mm});
            skLineSegment(sketch, "E51.15.0.1", {"start": v(2444.17, 55.54) * mm, "end": v(2445, 56.12) * mm});
            skLineSegment(sketch, "E51.16.0.0", {"start": v(2456.51, 57.18) * mm, "end": v(2457.35, 57.75) * mm});
            skLineSegment(sketch, "E51.16.0.1", {"start": v(2457.67, 55.54) * mm, "end": v(2458.5, 56.12) * mm});
            skLineSegment(sketch, "E51.17.0.0", {"start": v(2470.01, 57.18) * mm, "end": v(2470.85, 57.75) * mm});
            skLineSegment(sketch, "E51.17.0.1", {"start": v(2471.17, 55.54) * mm, "end": v(2472, 56.12) * mm});
            skLineSegment(sketch, "E51.18.0.0", {"start": v(2483.51, 57.18) * mm, "end": v(2484.35, 57.75) * mm});
            skLineSegment(sketch, "E51.18.0.1", {"start": v(2484.67, 55.54) * mm, "end": v(2485.5, 56.12) * mm});
            skLineSegment(sketch, "E51.19.0.0", {"start": v(2497.01, 57.18) * mm, "end": v(2497.85, 57.75) * mm});
            skLineSegment(sketch, "E51.19.0.1", {"start": v(2498.17, 55.54) * mm, "end": v(2499, 56.12) * mm});
            skLineSegment(sketch, "E51.20.0.0", {"start": v(2510.51, 57.18) * mm, "end": v(2511.35, 57.75) * mm});
            skLineSegment(sketch, "E51.20.0.1", {"start": v(2511.67, 55.54) * mm, "end": v(2512.5, 56.12) * mm});
            skLineSegment(sketch, "E51.21.0.0", {"start": v(2524.01, 57.18) * mm, "end": v(2524.85, 57.75) * mm});
            skLineSegment(sketch, "E51.21.0.1", {"start": v(2525.17, 55.54) * mm, "end": v(2526, 56.12) * mm});
            skLineSegment(sketch, "E51.22.0.0", {"start": v(2537.51, 57.18) * mm, "end": v(2538.35, 57.75) * mm});
            skLineSegment(sketch, "E51.22.0.1", {"start": v(2538.67, 55.54) * mm, "end": v(2539.5, 56.12) * mm});
            skLineSegment(sketch, "E51.23.0.0", {"start": v(2551.01, 57.18) * mm, "end": v(2551.85, 57.75) * mm});
            skLineSegment(sketch, "E51.23.0.1", {"start": v(2552.17, 55.54) * mm, "end": v(2553, 56.12) * mm});
            skLineSegment(sketch, "E51.24.0.0", {"start": v(2564.51, 57.18) * mm, "end": v(2565.35, 57.75) * mm});
            skLineSegment(sketch, "E51.24.0.1", {"start": v(2565.67, 55.54) * mm, "end": v(2566.5, 56.12) * mm});
            skLineSegment(sketch, "E51.25.0.0", {"start": v(2578.01, 57.18) * mm, "end": v(2578.85, 57.75) * mm});
            skLineSegment(sketch, "E51.25.0.1", {"start": v(2579.17, 55.54) * mm, "end": v(2580, 56.12) * mm});
            skLineSegment(sketch, "E51.26.0.0", {"start": v(2591.51, 57.18) * mm, "end": v(2592.35, 57.75) * mm});
            skLineSegment(sketch, "E51.26.0.1", {"start": v(2592.67, 55.54) * mm, "end": v(2593.5, 56.12) * mm});
            skLineSegment(sketch, "E51.27.0.0", {"start": v(2605.01, 57.18) * mm, "end": v(2605.85, 57.75) * mm});
            skLineSegment(sketch, "E51.27.0.1", {"start": v(2606.17, 55.54) * mm, "end": v(2607, 56.12) * mm});
            skLineSegment(sketch, "E51.28.0.0", {"start": v(2618.51, 57.18) * mm, "end": v(2619.35, 57.75) * mm});
            skLineSegment(sketch, "E51.28.0.1", {"start": v(2619.67, 55.54) * mm, "end": v(2620.5, 56.12) * mm});
            skLineSegment(sketch, "E51.29.0.0", {"start": v(2632.01, 57.18) * mm, "end": v(2632.85, 57.75) * mm});
            skLineSegment(sketch, "E51.29.0.1", {"start": v(2633.17, 55.54) * mm, "end": v(2634, 56.12) * mm});
            skLineSegment(sketch, "E51.30.0.0", {"start": v(2645.51, 57.18) * mm, "end": v(2646.35, 57.75) * mm});
            skLineSegment(sketch, "E51.30.0.1", {"start": v(2646.67, 55.54) * mm, "end": v(2647.5, 56.12) * mm});
            skLineSegment(sketch, "E51.31.0.0", {"start": v(2659.01, 57.18) * mm, "end": v(2659.85, 57.75) * mm});
            skLineSegment(sketch, "E51.31.0.1", {"start": v(2660.17, 55.54) * mm, "end": v(2661, 56.12) * mm});
            skLineSegment(sketch, "E51.32.0.0", {"start": v(2672.51, 57.18) * mm, "end": v(2673.35, 57.75) * mm});
            skLineSegment(sketch, "E51.32.0.1", {"start": v(2673.67, 55.54) * mm, "end": v(2674.5, 56.12) * mm});
            skLineSegment(sketch, "E51.33.0.0", {"start": v(2686.01, 57.18) * mm, "end": v(2686.85, 57.75) * mm});
            skLineSegment(sketch, "E51.33.0.1", {"start": v(2687.17, 55.54) * mm, "end": v(2688, 56.12) * mm});
            skLineSegment(sketch, "E51.direction1", {"start": v(2240.51, 57.18) * mm, "end": v(2254.01, 57.18) * mm, "construction": true});
            skLineSegment(sketch, "E52", {"start": v(2699.51, 57.18) * mm, "end": v(2700.67, 55.54) * mm});
            skLineSegment(sketch, "E53", {"start": v(2170.09, -2.85) * mm, "end": v(2741.09, -2.85) * mm});
            skLineSegment(sketch, "E54", {"start": v(2169.08, 107.77) * mm, "end": v(2741.09, 107.77) * mm});
            skLineSegment(sketch, "E55", {"start": v(2169.08, 107.77) * mm, "end": v(2167.08, 107.77) * mm});
            skLineSegment(sketch, "E56", {"start": v(2167.08, 107.77) * mm, "end": v(2167.08, -2.85) * mm});
            skLineSegment(sketch, "E57", {"start": v(2167.08, -2.85) * mm, "end": v(2170.09, -2.85) * mm});
            skLineSegment(sketch, "E58", {"start": v(2741.09, 107.77) * mm, "end": v(2743.09, 107.77) * mm});
            skLineSegment(sketch, "E59", {"start": v(2743.09, 107.77) * mm, "end": v(2743.09, -2.85) * mm});
            skLineSegment(sketch, "E60", {"start": v(2743.09, -2.85) * mm, "end": v(2741.09, -2.85) * mm});
            skSolve(sketch);
        }
        {
            var Q0;
            Q0 = qSketchRegion(id + "F22", true);
            extrude(context, id + "F23", {"entities" : qUnion([Q0]), "operationType" : NewBodyOperationType.REMOVE, "oppositeDirection" : true, "depth" : 140 * mm, "offsetDistance" : 25 * mm});
        }
        {
            var Q0;
            Q0=qCreatedBy(makeId("Top.planeOp"),FACE);
            var sketch = newSketch(context, id + "F24", { "sketchPlane" : qUnion([Q0]), "disableImprinting" : false});
            skLineSegment(sketch, "E61.bottom", {"start": v(-1957.94, -3) * mm, "end": v(-1367.94, -3) * mm});
            skLineSegment(sketch, "E61.top", {"start": v(-1957.94, 3) * mm, "end": v(-1367.94, 3) * mm});
            skLineSegment(sketch, "E61.left", {"start": v(-1957.94, -3) * mm, "end": v(-1957.94, 3) * mm});
            skLineSegment(sketch, "E61.right", {"start": v(-1367.94, -3) * mm, "end": v(-1367.94, 3) * mm});
            skPoint(sketch, "E61.middle", {"position": v(-1662.94, 0) * mm});
            skSolve(sketch);
        }
        {
            var Q0;
            Q0 = qSketchRegion(id + "F24", true);
            extrude(context, id + "F25", {"entities" : qUnion([Q0]), "flatOperationType" : FlatOperationType.REMOVE, "depth" : 330 * mm, "offsetDistance" : 25 * mm, "domain" : OperationDomain.MODEL});
        }
        {
            var Q0;
            Q0=qCreatedBy(makeId("Top.planeOp"),FACE);
            var sketch = newSketch(context, id + "F26", { "sketchPlane" : qUnion([Q0])});
            skLineSegment(sketch, "E62.bottom", {"start": v(1090, -25) * mm, "end": v(1140, -25) * mm});
            skLineSegment(sketch, "E62.top", {"start": v(1090, 25) * mm, "end": v(1140, 25) * mm});
            skLineSegment(sketch, "E62.left", {"start": v(1090, -25) * mm, "end": v(1090, 25) * mm});
            skLineSegment(sketch, "E62.right", {"start": v(1140, -25) * mm, "end": v(1140, 25) * mm});
            skPoint(sketch, "E62.middle", {"position": v(1115, 0) * mm});
            skSolve(sketch);
        }
        {
            var Q0;
            Q0 = qSketchRegion(id + "F26", true);
            extrude(context, id + "F27", {"entities" : qUnion([Q0]), "depth" : 85 * mm, "offsetDistance" : 25 * mm});
        }
        {
            var Q0;
            Q0=qCreatedBy(makeId("Front.planeOp"),FACE);
            var sketch = newSketch(context, id + "F28", { "sketchPlane" : qUnion([Q0])});
            skLineSegment(sketch, "E63", {"start": v(1115, 109.3) * mm, "end": v(1115, -30.7) * mm, "construction": true});
            skSolve(sketch);
        }
        {
            var Q0;
            Q0=qCreatedBy(makeId("Front.planeOp"),FACE);
            var sketch = newSketch(context, id + "F29", { "sketchPlane" : qUnion([Q0])});
            skLineSegment(sketch, "E64.bottom", {"start": v(1157.5, 0) * mm, "end": v(1127.5, 0) * mm});
            skLineSegment(sketch, "E64.top", {"start": v(1157.5, 80) * mm, "end": v(1127.5, 80) * mm});
            skLineSegment(sketch, "E64.left", {"start": v(1157.5, 0) * mm, "end": v(1157.5, 80) * mm});
            skLineSegment(sketch, "E64.right", {"start": v(1127.5, 0) * mm, "end": v(1127.5, 80) * mm});
            skSolve(sketch);
        }
        {
            var Q0;
            Q0 = qSketchRegion(id + "F29", true);
            var Q1;
            Q1=sQuery(id+"F28.wireOp",EDGE,"E63");
            revolve(context, id + "F30", {"operationType" : NewBodyOperationType.REMOVE, "surfaceOperationType" : NewSurfaceOperationType.NEW, "entities" : qUnion([Q0]), "axis" : qUnion([Q1]), "revolveType" : RevolveType.FULL, "oppositeDirection" : true});
        }
    });
